# Revit family: DOT BLOCK SURFACE 964_DM40W9.3
name_source: partatom
category: Luminarias
units: mm (PartAtom-declared; Revit-internal decimal feet)

## family parameters
Compartido = No
Corte con vacíos al cargar = No
Cota de conector redondo = Diámetro de uso
Origen de luz = Sí
Punto de cálculo de habitación = No
Se basa en plano de trabajo = Sí
Siempre vertical = Sí
Tipo de pieza = Normal

## types (1)
- DOT BLOCK SURFACE 964_DM40W9.3.1535
    Archivo de red fotométrica = L964A-40W-830-B-15X35_IESNA95.IES
    Cambio de temperatura de color de luz atenuada = <Ninguno>
    Comentarios de vataje = 90-240V
    Descripción = LUMINARIA DOWNLIGHT EN FORMATO RECTANGULAR PARA EMPOTRAR DIRECTO EN PLAFON, CUERPO DE ALUMINIO ACABADO EN COLOR NEGRO, IP 20, PESO 1.98Kg, TIPO DE LED 3030SMD PHILIPS CON 44W TOTAL, 3150 LUMENES, 81LM/W, IRC 90, TEMPERATURA EN BLANCO CALIDO 3000K, 50 MIL HORAS DE VIDA PROMEDIO, APERTURA ELIPTICA DE 15X35 GRADOS POR PROYECTO, ALIMENTADO A 90-240V
    Elevación por defecto = 1219 mm
    Fabricante = BRILLANT
    Filtro de color = 16777215
    Lámpara = 3030SMD PHILIPS
    Modelo = DM40W.9.3.1535
    Watt per fixture = 44
    Ángulo de inclinación = 60.00°

## geometry (parser evidence)
native form markers: Blend x2
no freeform markers — native parametric forms only
